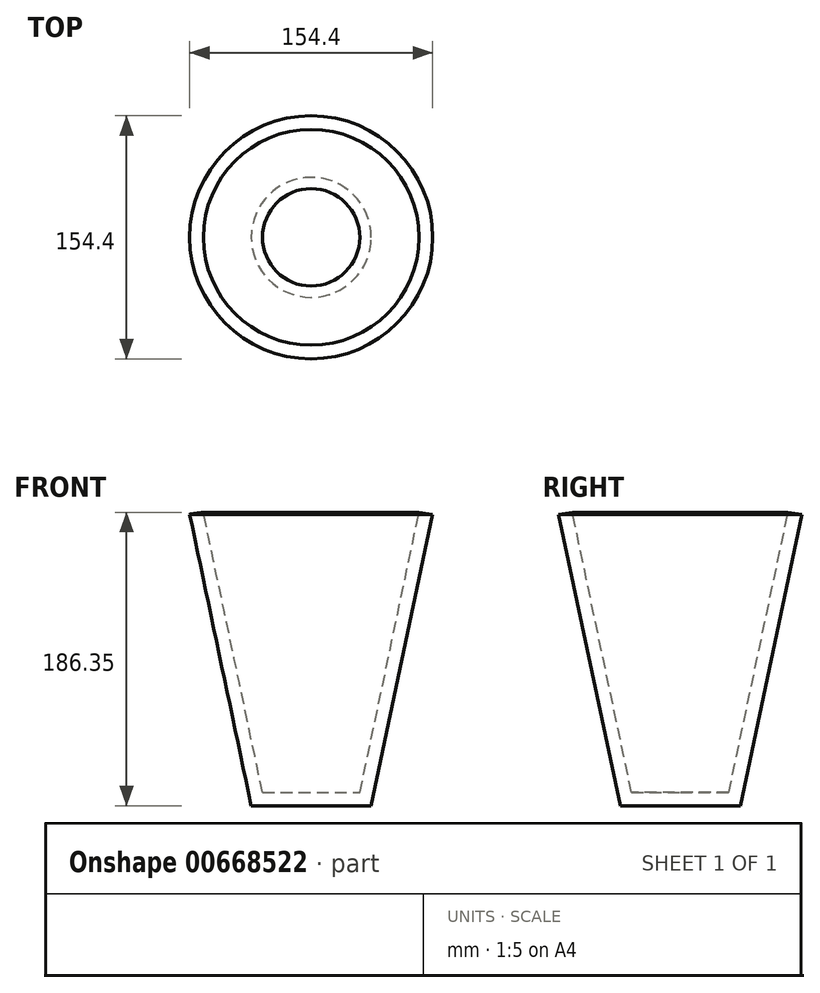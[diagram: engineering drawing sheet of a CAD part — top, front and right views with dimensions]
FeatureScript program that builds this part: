
annotation { "Feature Type Name" : "Feature", "Feature Type Description" : "" }
export const myFeature = defineFeature(function(context is Context, id is Id, definition is map)
    precondition{}
    {
        {
            var Q0;
            Q0=qCreatedBy(makeId("Front.planeOp"),FACE);
            var sketch = newSketch(context, id + "F0", { "sketchPlane" : qUnion([Q0])});
            skLineSegment(sketch, "E0", {"start": v(-77.2, 106.52) * mm, "end": v(-38.1, -78.6) * mm});
            skLineSegment(sketch, "E1", {"start": v(-38.1, -78.6) * mm, "end": v(0, -78.6) * mm});
            skLineSegment(sketch, "E2", {"start": v(0, -78.6) * mm, "end": v(0, -70.22) * mm});
            skLineSegment(sketch, "E3", {"start": v(0, -70.22) * mm, "end": v(-30.92, -70.22) * mm});
            skLineSegment(sketch, "E4", {"start": v(-30.92, -70.22) * mm, "end": v(-68.5, 107.76) * mm});
            skLineSegment(sketch, "E5", {"start": v(-68.5, 107.76) * mm, "end": v(-77.2, 106.52) * mm});
            skSolve(sketch);
        }
        {
            var Q0;
            Q0 = qSketchRegion(id + "F0", true);
            var Q1;
            Q1=sQuery(id+"F0.wireOp",EDGE,"E2");
            revolve(context, id + "F1", {"entities" : qUnion([Q0]), "axis" : qUnion([Q1]), "revolveType" : RevolveType.FULL});
        }
    });
